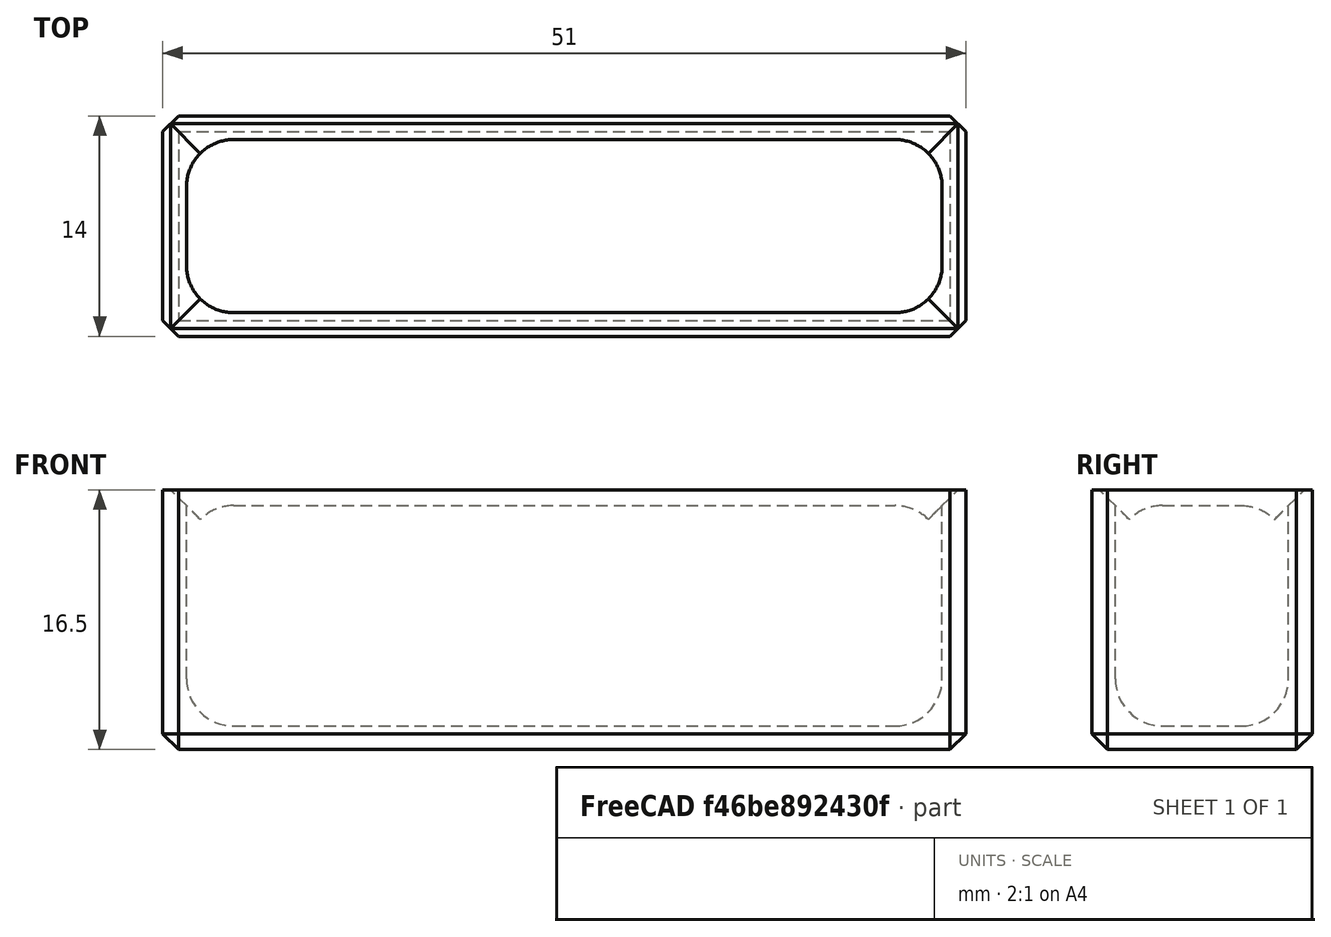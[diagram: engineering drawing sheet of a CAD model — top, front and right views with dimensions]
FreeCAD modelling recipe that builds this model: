
FCSTD DOCUMENT  (FreeCAD 1.0R39319 (Git))
Label: fillamentCutterSheath
License: All rights reserved
LicenseURL: https://en.wikipedia.org/wiki/All_rights_reserved
objects: PartDesign::AdditiveBox×1, PartDesign::Thickness×1, PartDesign::Chamfer×1, PartDesign::Fillet×1, PartDesign::Body×1
note: 13 computed .brp shape members not serialized (recipe doc carries the construction recipe); baked Part::Feature solids carry a one-line shape summary decoded from their .brp

FEATURE [PartDesign::AdditiveBox] Box
  AttacherType = Attacher::AttachEngine3D
  AttachmentSupport = -> [XY_Plane]
  Height = 15
  Length = 48
  MapMode = 5
  Refine = true
  Suppressed = false
  Width = 11
FEATURE [PartDesign::Thickness] Thickness
  Base = -> Box [Face6]
  BaseFeature = -> Box
  Intersection = false
  Join = 1
  Mode = 0
  Refine = true
  SupportTransform = false
  Suppressed = false
  Value = 1.5
FEATURE [PartDesign::Chamfer] Chamfer
  Angle = 45
  Base = -> Thickness [Edge2,Edge12,Edge6,Edge8,Edge19,Edge18,Edge23,Edge20,Edge22,Edge21,Edge24,Edge17]
  BaseFeature = -> Thickness
  ChamferType = 0
  FlipDirection = false
  Refine = true
  Size = 0.99999
  Size2 = 1
  SupportTransform = false
  Suppressed = false
  UseAllEdges = false
FEATURE [PartDesign::Fillet] Fillet
  Base = -> Chamfer [Edge4,Edge14,Edge7,Edge11,Edge6,Edge12,Edge1,Edge3]
  BaseFeature = -> Chamfer
  Radius = 3
  Refine = true
  SupportTransform = false
  Suppressed = false
  UseAllEdges = false
FEATURE [PartDesign::Body] Body
  AllowCompound = false
  Group = -> [Box,Thickness,Chamfer,Fillet]
  Origin = -> Origin
  Tip = -> Fillet
